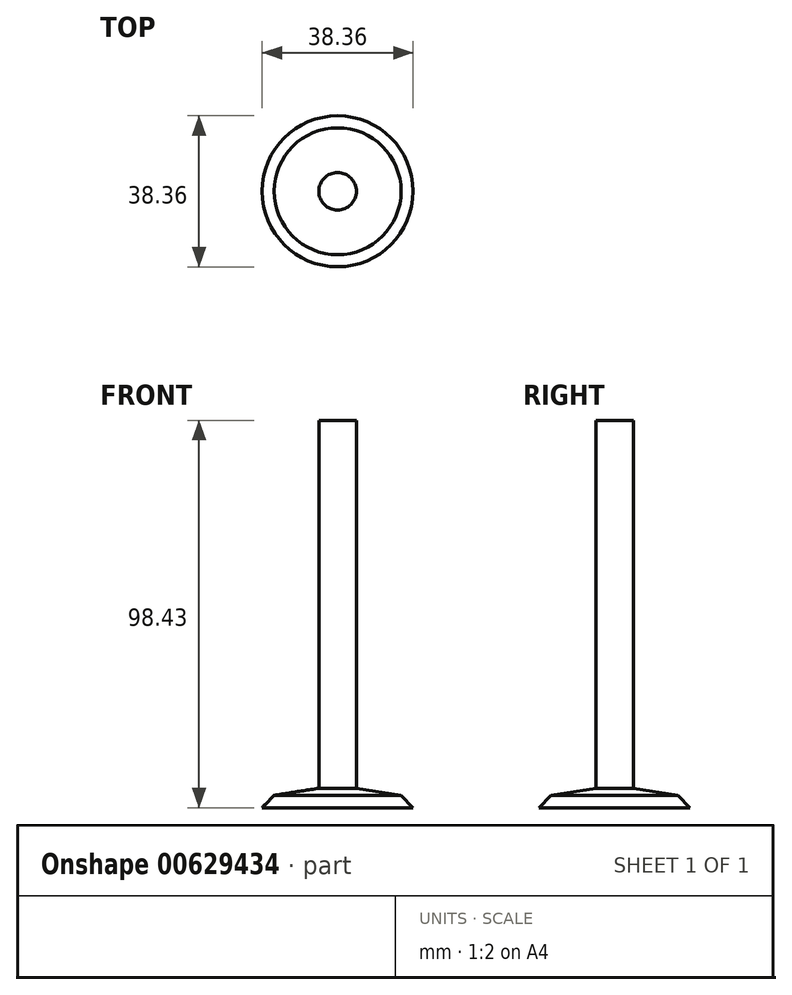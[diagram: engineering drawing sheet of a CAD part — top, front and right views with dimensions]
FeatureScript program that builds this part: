
annotation { "Feature Type Name" : "Feature", "Feature Type Description" : "" }
export const myFeature = defineFeature(function(context is Context, id is Id, definition is map)
    precondition{}
    {
        {
            var Q0;
            Q0=qCreatedBy(makeId("Top.planeOp"),FACE);
            var sketch = newSketch(context, id + "F0", { "sketchPlane" : qUnion([Q0])});
            skCircle(sketch, "E0", {"center": v(0, 0) * mm, "radius": 25.65 * mm});
            skSolve(sketch);
        }
        {
            var Q0;
            Q0=qCreatedBy(makeId("Front.planeOp"),FACE);
            var sketch = newSketch(context, id + "F1", { "sketchPlane" : qUnion([Q0])});
            skLineSegment(sketch, "E1", {"start": v(0, 0) * mm, "end": v(19.18, 0) * mm});
            skLineSegment(sketch, "E2", {"start": v(19.18, 0) * mm, "end": v(16.12, 3.14) * mm});
            skLineSegment(sketch, "E3.bottom", {"start": v(-4.76, 69.85) * mm, "end": v(4.76, 69.85) * mm});
            skLineSegment(sketch, "E3.top", {"start": v(-4.76, -69.85) * mm, "end": v(4.76, -69.85) * mm});
            skLineSegment(sketch, "E3.left", {"start": v(-4.76, 69.85) * mm, "end": v(-4.76, -69.85) * mm});
            skLineSegment(sketch, "E3.right", {"start": v(4.76, 69.85) * mm, "end": v(4.76, 4.95) * mm});
            skPoint(sketch, "E3.middle", {"position": v(0, 0) * mm});
            skLineSegment(sketch, "E4", {"start": v(16.12, 3.14) * mm, "end": v(4.76, 4.95) * mm});
            skLineSegment(sketch, "E5", {"start": v(0, 0) * mm, "end": v(-4.76, 0) * mm});
            skLineSegment(sketch, "E6.MirrorCS", {"start": v(-16.12, 3.14) * mm, "end": v(-4.76, 4.95) * mm});
            skLineSegment(sketch, "E7.MirrorCS", {"start": v(-19.18, 0) * mm, "end": v(-16.12, 3.14) * mm});
            skLineSegment(sketch, "E8.MirrorCS", {"start": v(0, 0) * mm, "end": v(-19.18, 0) * mm});
            skLineSegment(sketch, "E9", {"start": v(0, 69.85) * mm, "end": v(0, -34.88) * mm});
            skSolve(sketch);
        }
        {
            var Q0;
            {var subQ4=sQuery(id+"F1.wireOp",EDGE,"E1");Q0=makeQuery(id+"F1.imprint","IMPRINT",FACE,{"disambiguationData":[TD([[makeQuery(id+"F1.imprint","IMPRINT",EDGE,{"derivedFrom":subQ4}),1.0]])]});}
            var Q1;
            Q1=sQuery(id+"F0.wireOp",EDGE,"E0");
            revolve(context, id + "F2", {"entities" : qUnion([Q0]), "axis" : qUnion([Q1]), "revolveType" : RevolveType.FULL});
        }
        {
            var Q0;
            Q0=makeQuery(id+"F2.opRevolve","SWEPT_FACE",FACE,{"disambiguationData":[OSD([sQuery(id+"F1.wireOp",EDGE,"E3.bottom")])]});
            extrude(context, id + "F3", {"entities" : qUnion([Q0]), "operationType" : NewBodyOperationType.ADD, "depth" : 50.8 * mm, "offsetDistance" : 25.4 * mm});
        }
        {
            var Q0;
            Q0=makeQuery(id+"F3.opExtrude","CAP_FACE",FACE,{"disambiguationData":[OSD([sQuery(id+"F1.wireOp",EDGE,"E3.bottom")])],"isStart":false});
            extrude(context, id + "F4", {"entities" : qUnion([Q0]), "operationType" : NewBodyOperationType.REMOVE, "oppositeDirection" : true, "depth" : 22.22 * mm, "offsetDistance" : 25.4 * mm});
        }
    });
